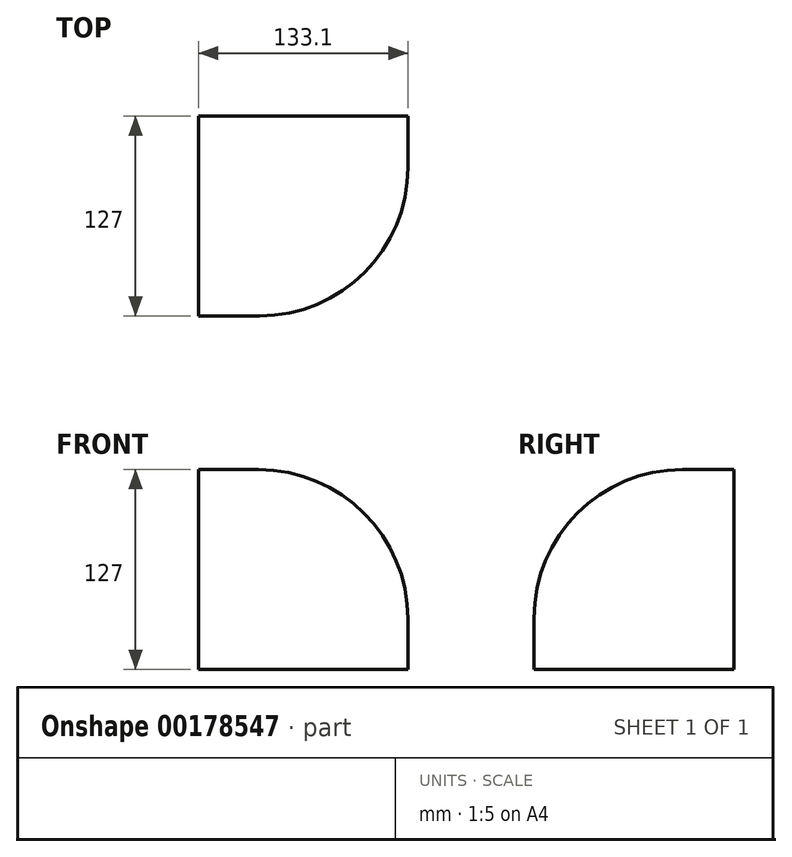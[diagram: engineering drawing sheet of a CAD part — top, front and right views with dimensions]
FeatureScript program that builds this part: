
annotation { "Feature Type Name" : "Feature", "Feature Type Description" : "" }
export const myFeature = defineFeature(function(context is Context, id is Id, definition is map)
    precondition{}
    {
        {
            var Q0;
            Q0=qCreatedBy(makeId("Right.planeOp"),FACE);
            var sketch = newSketch(context, id + "F0", { "sketchPlane" : qUnion([Q0])});
            skLineSegment(sketch, "E0.bottom", {"start": v(0, 0) * mm, "end": v(127, 0) * mm});
            skLineSegment(sketch, "E0.top", {"start": v(0, 127) * mm, "end": v(127, 127) * mm});
            skLineSegment(sketch, "E0.left", {"start": v(0, 0) * mm, "end": v(0, 127) * mm});
            skLineSegment(sketch, "E0.right", {"start": v(127, 0) * mm, "end": v(127, 127) * mm});
            skSolve(sketch);
        }
        {
            var Q0;
            Q0 = qSketchRegion(id + "F0", true);
            extrude(context, id + "F1", {"entities" : qUnion([Q0]), "depth" : 133.1 * mm});
        }
        {
            var Q0;
            Q0=makeQuery(id+"F1.opExtrude","CAP_EDGE",EDGE,{"disambiguationData":[OSD([sQuery(id+"F0.wireOp",EDGE,"E0.top")])],"isStart":false});
            fillet(context, id + "F2", {"entities" : qUnion([Q0]), "radius" : 95.05 * mm, "tangentPropagation" : true, "allowEdgeOverflow" : false});
        }
        {
            var Q0;
            Q0=makeQuery(id+"F2.opFillet","BLEND_EDGE",EDGE,{"blendedFrom":[makeQuery(id+"F1.opExtrude","CAP_EDGE",EDGE,{"disambiguationData":[OSD([sQuery(id+"F0.wireOp",EDGE,"E0.top")])],"isStart":false}),makeQuery(id+"F1.opExtrude","SWEPT_FACE",FACE,{"disambiguationData":[OSD([sQuery(id+"F0.wireOp",EDGE,"E0.left")])]})],"blendedInto":[makeQuery(id+"F1.opExtrude","SWEPT_FACE",FACE,{"disambiguationData":[OSD([sQuery(id+"F0.wireOp",EDGE,"E0.left")])]})]});
            fillet(context, id + "F3", {"entities" : qUnion([Q0]), "radius" : 94.43 * mm, "tangentPropagation" : true, "allowEdgeOverflow" : false});
        }
    });
